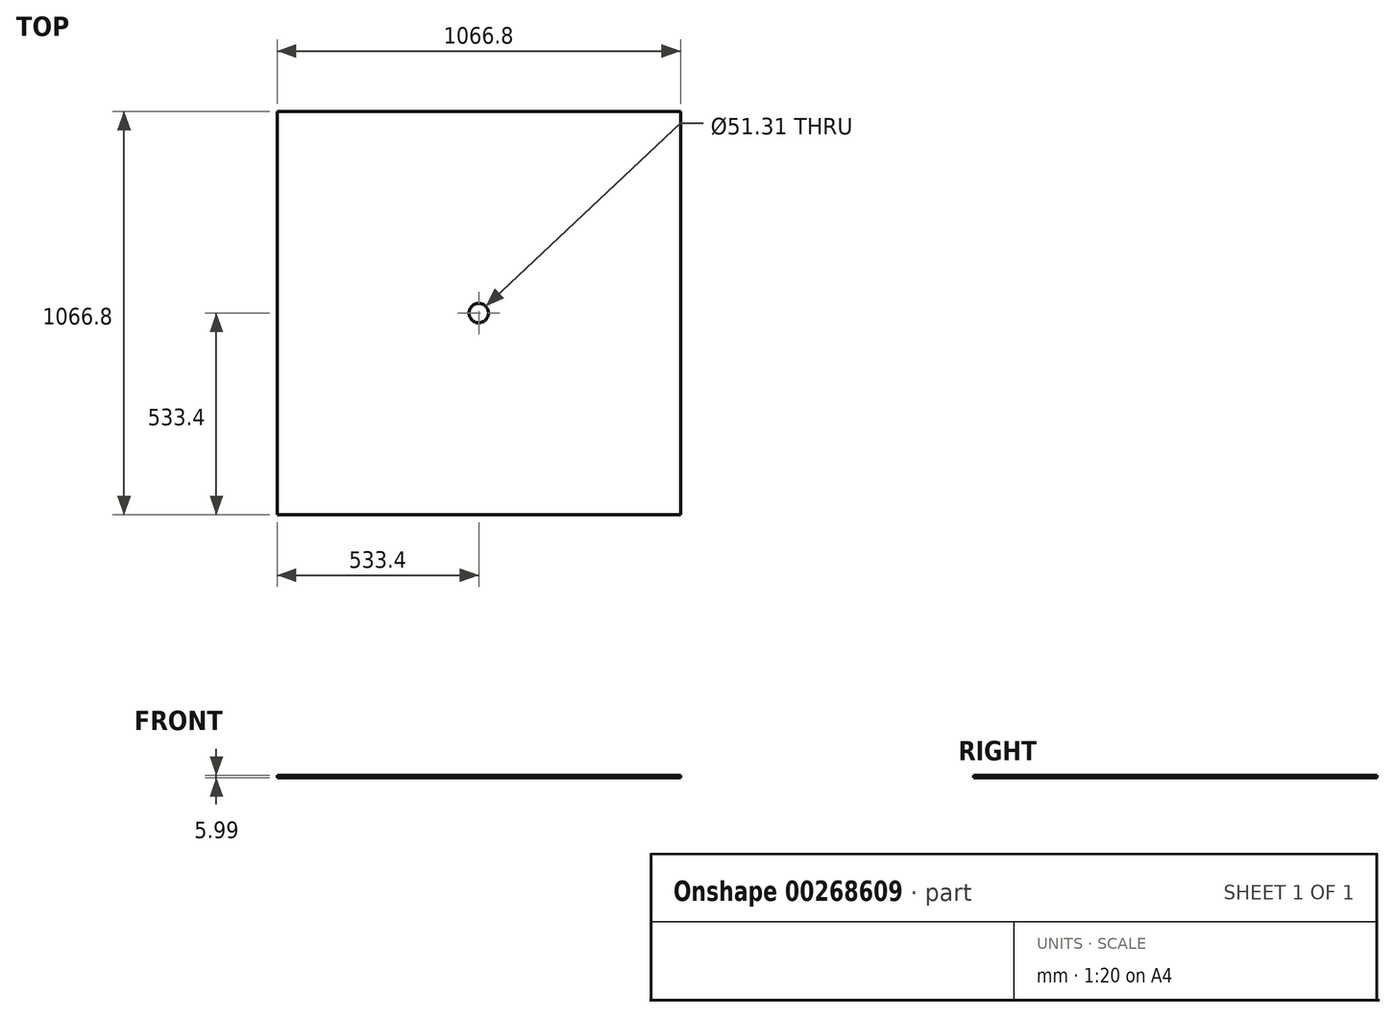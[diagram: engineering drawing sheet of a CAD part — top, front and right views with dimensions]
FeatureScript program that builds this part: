
annotation { "Feature Type Name" : "Feature", "Feature Type Description" : "" }
export const myFeature = defineFeature(function(context is Context, id is Id, definition is map)
    precondition{}
    {
        {
            var Q0;
            Q0=qCreatedBy(makeId("Top.planeOp"),FACE);
            var sketch = newSketch(context, id + "F0", { "sketchPlane" : qUnion([Q0])});
            skLineSegment(sketch, "E0.bottom", {"start": v(533.4, -533.4) * mm, "end": v(-533.4, -533.4) * mm});
            skLineSegment(sketch, "E0.top", {"start": v(533.4, 533.4) * mm, "end": v(-533.4, 533.4) * mm});
            skLineSegment(sketch, "E0.left", {"start": v(533.4, -533.4) * mm, "end": v(533.4, 533.4) * mm});
            skLineSegment(sketch, "E0.right", {"start": v(-533.4, -533.4) * mm, "end": v(-533.4, 533.4) * mm});
            skPoint(sketch, "E0.middle", {"position": v(0, 0) * mm});
            skCircle(sketch, "E1", {"center": v(0, 0) * mm, "radius": 25.65 * mm});
            skSolve(sketch);
        }
        {
            var Q0;
            Q0=makeQuery(id+"F0.imprint","IMPRINT",FACE,{"disambiguationData":[TD([[makeQuery(id+"F0.imprint","IMPRINT",EDGE,{"derivedFrom":sQuery(id+"F0.wireOp",EDGE,"E0.bottom")}),-1.0]])]});
            extrude(context, id + "F1", {"entities" : qUnion([Q0]), "depth" : 6 * mm});
        }
    });
